# Revit family: RBA2729-232
name_source: partatom
category: Plumbing Fixtures
revit_build: Autodesk Revit 2015 (Build: 20140223_1515(x64)
units: mm (PartAtom-declared; Revit-internal decimal feet)

## types (3) — shared parameters
CW Connection = Yes
CWFU = 1.5
Default Elevation = 838 mm
HW Connection = No
Manufacturer = RBA Group
Material = Stainless Steel Satin Finish
URL = http://www.rba.com.au
Vent Connection = No
WFU = 2
Waste Connection = Yes
zero-valued in all types: HWFU

## per-type parameters (varying)
| type | Description |
| rba2729-232 | 'Contour' Double Water Cooler, 30L/hr 1.2mm Type 304 Stainless Steel |
| rba2729-332 | 'Contour' Double Water Cooler, with Glass Filler 30L/hr 1.2mm Type 304 Stainless Steel |
| rba2729-933 | 'Contour' Heavy Duty Water Cooler, 30L/hr 2.0mm Type 304 Stainless Steel |

note: column(s) folded — value = type name in every type: Model

## geometry (parser evidence)
native form markers: Blend x10, Sweep x8
no freeform markers — native parametric forms only
